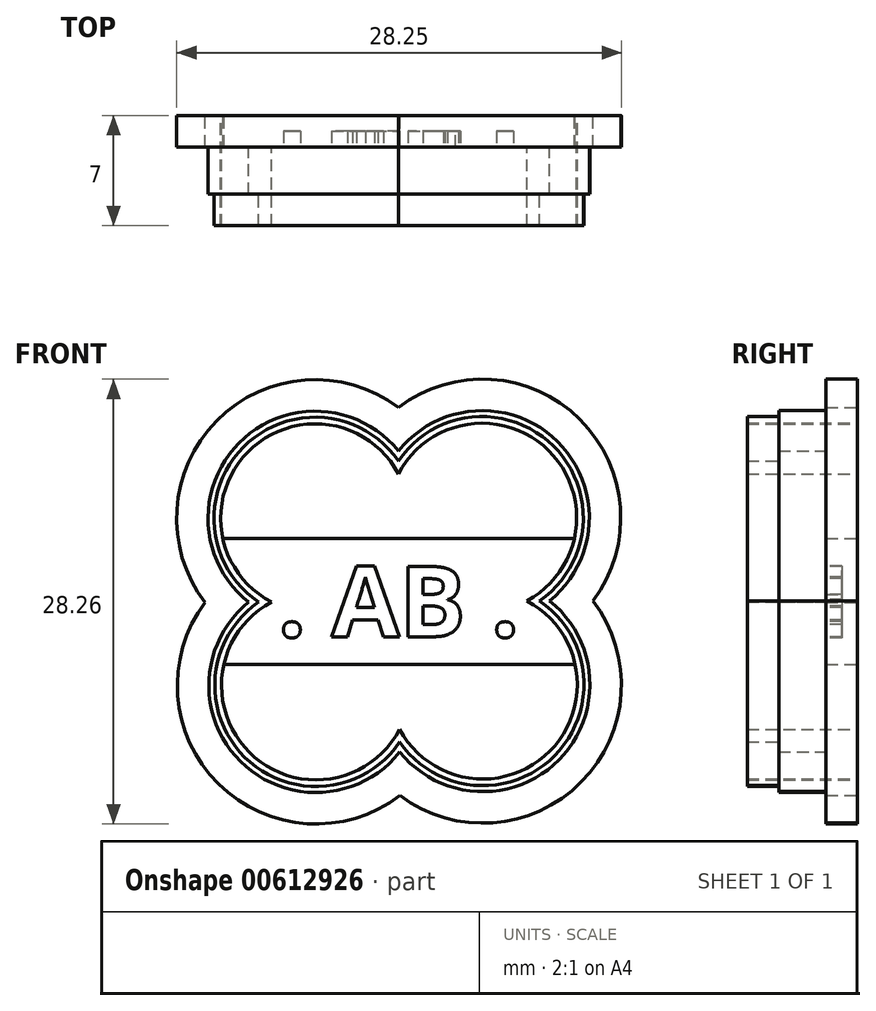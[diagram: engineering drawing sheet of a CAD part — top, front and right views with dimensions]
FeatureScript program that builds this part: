
annotation { "Feature Type Name" : "Feature", "Feature Type Description" : "" }
export const myFeature = defineFeature(function(context is Context, id is Id, definition is map)
    precondition{}
    {
        {
            var Q0;
            Q0=qCreatedBy(makeId("Front.planeOp"),FACE);
            var sketch = newSketch(context, id + "F0", { "sketchPlane" : qUnion([Q0])});
            skArc(sketch, "E0", {"start": v(-0.03, 8.1) * mm, "mid": v(-9.59, 9.5) * mm, "end": v(-8.1, -0.04) * mm});
            skArc(sketch, "E1", {"start": v(-8.1, -0.04) * mm, "mid": v(-9.5, -9.6) * mm, "end": v(0.04, -8.12) * mm});
            skArc(sketch, "E2.trimOffspring", {"start": v(8.12, 0.03) * mm, "mid": v(9.5, 9.58) * mm, "end": v(-0.03, 8.1) * mm});
            skArc(sketch, "E3.trimOffspring", {"start": v(0.04, -8.12) * mm, "mid": v(9.59, -9.5) * mm, "end": v(8.12, 0.03) * mm});
            skArc(sketch, "E4.0", {"start": v(-0.03, 8.92) * mm, "mid": v(-9.89, 9.8) * mm, "end": v(-8.9, -0.04) * mm});
            skArc(sketch, "E4.1", {"start": v(8.93, 0.03) * mm, "mid": v(9.8, 9.88) * mm, "end": v(-0.03, 8.92) * mm});
            skArc(sketch, "E4.2", {"start": v(0.05, -8.93) * mm, "mid": v(9.89, -9.8) * mm, "end": v(8.93, 0.03) * mm});
            skArc(sketch, "E4.3", {"start": v(-8.9, -0.04) * mm, "mid": v(-9.8, -9.9) * mm, "end": v(0.05, -8.93) * mm});
            skSolve(sketch);
        }
        {
            var Q0;
            Q0=qSketchRegion(id+"F0",true);
            extrude(context, id + "F1", {"entities" : qUnion([Q0]), "depth" : 7 * mm, "offsetDistance" : 25 * mm});
        }
        {
            var Q0;
            Q0=qCreatedBy(makeId("Front.planeOp"),FACE);
            var sketch = newSketch(context, id + "F2", { "sketchPlane" : qUnion([Q0])});
            skArc(sketch, "E5.0", {"start": v(-9.55, -0.05) * mm, "mid": v(-10.06, -10.16) * mm, "end": v(0.05, -9.57) * mm});
            skArc(sketch, "E5.1", {"start": v(-0.03, 9.56) * mm, "mid": v(-10.15, 10.07) * mm, "end": v(-9.55, -0.05) * mm});
            skArc(sketch, "E5.2", {"start": v(9.57, 0.04) * mm, "mid": v(10.07, 10.15) * mm, "end": v(-0.03, 9.56) * mm});
            skArc(sketch, "E5.3", {"start": v(0.05, -9.57) * mm, "mid": v(10.16, -10.07) * mm, "end": v(9.57, 0.04) * mm});
            skSolve(sketch);
        }
        {
            var Q0;
            Q0=qSketchRegion(id+"F2",true);
            extrude(context, id + "F3", {"entities" : qUnion([Q0]), "operationType" : NewBodyOperationType.ADD, "depth" : 5 * mm, "offsetDistance" : 25 * mm});
        }
        {
            var Q0;
            Q0=makeQuery(id+"F3.boolean.opBoolean","SPLIT",FACE,{"disambiguationData":[TD([makeQuery(id+"F1.opExtrude","SWEPT_FACE",FACE,{"disambiguationData":[OSD([sQuery(id+"F0.wireOp",EDGE,"E0")])]})])],"derivedFrom":makeQuery(id+"F3.opExtrude","CAP_FACE",FACE,{"disambiguationData":[OSD([sQuery(id+"F2.wireOp",EDGE,"E5.0"),sQuery(id+"F2.wireOp",EDGE,"E5.1"),sQuery(id+"F2.wireOp",EDGE,"E5.2"),sQuery(id+"F2.wireOp",EDGE,"E5.3")])],"isStart":false})});
            var sketch = newSketch(context, id + "F4", { "sketchPlane" : qUnion([Q0])});
            skSolve(sketch);
        }
        {
            var Q0;
            {var subQ0=makeQuery(id+"F3.opExtrude","CAP_FACE",FACE,{"disambiguationData":[OSD([sQuery(id+"F2.wireOp",EDGE,"E5.0"),sQuery(id+"F2.wireOp",EDGE,"E5.1"),sQuery(id+"F2.wireOp",EDGE,"E5.2"),sQuery(id+"F2.wireOp",EDGE,"E5.3")])],"isStart":false});Q0=makeQuery(id+"F4.imprint","IMPRINT",FACE,{"disambiguationData":[TD([[makeQuery(id+"F4.imprint","IMPRINT",EDGE,{"derivedFrom":makeQuery(id+"F3.boolean.opBoolean","INTERSECT",EDGE,{"derivedFrom":[makeQuery(id+"F1.opExtrude","SWEPT_FACE",FACE,{"disambiguationData":[OSD([sQuery(id+"F0.wireOp",EDGE,"E0")])]}),subQ0]})}),1.0]])]});}
            extrude(context, id + "F5", {"entities" : qUnion([Q0]), "operationType" : NewBodyOperationType.REMOVE, "oppositeDirection" : true, "depth" : 8 * mm, "offsetDistance" : 25 * mm});
        }
        {
            var Q0;
            Q0=qCreatedBy(makeId("Front.planeOp"),FACE);
            var sketch = newSketch(context, id + "F6", { "sketchPlane" : qUnion([Q0])});
            skArc(sketch, "E6.0", {"start": v(-12.31, -0.06) * mm, "mid": v(-11.47, -11.59) * mm, "end": v(0.07, -12.33) * mm});
            skArc(sketch, "E6.1", {"start": v(-0.04, 12.32) * mm, "mid": v(-11.57, 11.48) * mm, "end": v(-12.31, -0.06) * mm});
            skArc(sketch, "E6.2", {"start": v(12.33, 0.05) * mm, "mid": v(11.48, 11.57) * mm, "end": v(-0.04, 12.32) * mm});
            skArc(sketch, "E6.3", {"start": v(0.07, -12.33) * mm, "mid": v(11.58, -11.47) * mm, "end": v(12.33, 0.05) * mm});
            skSolve(sketch);
        }
        {
            var Q0;
            Q0=qSketchRegion(id+"F6",true);
            extrude(context, id + "F7", {"entities" : qUnion([Q0]), "operationType" : NewBodyOperationType.ADD, "depth" : 2 * mm, "offsetDistance" : 25 * mm});
        }
        {
            var Q0;
            {var subQ3=sQuery(id+"F0.wireOp",EDGE,"E0");Q0=makeQuery(id+"F7.boolean.opBoolean","SPLIT",FACE,{"disambiguationData":[TD([makeQuery(id+"F1.opExtrude","SWEPT_FACE",FACE,{"disambiguationData":[OSD([subQ3])]})])],"derivedFrom":makeQuery(id+"F7.opExtrude","CAP_FACE",FACE,{"disambiguationData":[OSD([sQuery(id+"F6.wireOp",EDGE,"E6.0"),sQuery(id+"F6.wireOp",EDGE,"E6.1"),sQuery(id+"F6.wireOp",EDGE,"E6.2"),sQuery(id+"F6.wireOp",EDGE,"E6.3")])],"isStart":false})});}
            var sketch = newSketch(context, id + "F8", { "sketchPlane" : qUnion([Q0])});
            skSolve(sketch);
        }
        {
            var Q0;
            {var subQ0=makeQuery(id+"F7.opExtrude","CAP_FACE",FACE,{"disambiguationData":[OSD([sQuery(id+"F6.wireOp",EDGE,"E6.0"),sQuery(id+"F6.wireOp",EDGE,"E6.1"),sQuery(id+"F6.wireOp",EDGE,"E6.2"),sQuery(id+"F6.wireOp",EDGE,"E6.3")])],"isStart":false});var subQ1=sQuery(id+"F2.wireOp",EDGE,"E5.3");var subQ2=sQuery(id+"F2.wireOp",EDGE,"E5.2");var subQ3=sQuery(id+"F2.wireOp",EDGE,"E5.1");var subQ4=sQuery(id+"F2.wireOp",EDGE,"E5.0");var subQ5=sQuery(id+"F0.wireOp",EDGE,"E0");Q0=makeQuery(id+"F8.imprint","IMPRINT",FACE,{"disambiguationData":[TD([[makeQuery(id+"F8.imprint","IMPRINT",EDGE,{"derivedFrom":makeQuery(id+"F7.boolean.opBoolean","INTERSECT",EDGE,{"derivedFrom":[makeQuery(id+"F5.boolean.opBoolean","MERGE",FACE,{"derivedFrom":[makeQuery(id+"F1.opExtrude","SWEPT_FACE",FACE,{"disambiguationData":[OSD([subQ5])]}),makeQuery(id+"F5.opExtrude","SWEPT_FACE",FACE,{"disambiguationData":[OSD([subQ5,subQ4,subQ3,subQ2,subQ1])]})]}),subQ0]})}),1.0]])]});}
            cPlane(context, id + "F9", {"entities" : qUnion([Q0]), "cplaneType" : CPlaneType.OFFSET, "offset" : 0 * mm, "width" : 150 * mm, "height" : 150 * mm});
        }
        {
            var Q0;
            {var subQ0=makeQuery(id+"F7.opExtrude","CAP_FACE",FACE,{"disambiguationData":[OSD([sQuery(id+"F6.wireOp",EDGE,"E6.0"),sQuery(id+"F6.wireOp",EDGE,"E6.1"),sQuery(id+"F6.wireOp",EDGE,"E6.2"),sQuery(id+"F6.wireOp",EDGE,"E6.3")])],"isStart":false});var subQ1=sQuery(id+"F2.wireOp",EDGE,"E5.3");var subQ2=sQuery(id+"F2.wireOp",EDGE,"E5.2");var subQ3=sQuery(id+"F2.wireOp",EDGE,"E5.1");var subQ4=sQuery(id+"F2.wireOp",EDGE,"E5.0");var subQ5=sQuery(id+"F0.wireOp",EDGE,"E0");Q0=makeQuery(id+"F8.imprint","IMPRINT",FACE,{"disambiguationData":[TD([[makeQuery(id+"F8.imprint","IMPRINT",EDGE,{"derivedFrom":makeQuery(id+"F7.boolean.opBoolean","INTERSECT",EDGE,{"derivedFrom":[makeQuery(id+"F5.boolean.opBoolean","MERGE",FACE,{"derivedFrom":[makeQuery(id+"F1.opExtrude","SWEPT_FACE",FACE,{"disambiguationData":[OSD([subQ5])]}),makeQuery(id+"F5.opExtrude","SWEPT_FACE",FACE,{"disambiguationData":[OSD([subQ5,subQ4,subQ3,subQ2,subQ1])]})]}),subQ0]})}),1.0]])]});}
            extrude(context, id + "F10", {"entities" : qUnion([Q0]), "operationType" : NewBodyOperationType.REMOVE, "oppositeDirection" : true, "depth" : 2 * mm, "offsetDistance" : 25 * mm});
        }
        {
            var Q0;
            Q0=qCreatedBy(id+"F9.planeOp",FACE);
            var sketch = newSketch(context, id + "F11", { "sketchPlane" : qUnion([Q0])});
            skLineSegment(sketch, "E7.bottom", {"start": v(-11.92, 0) * mm, "end": v(11.56, 0) * mm});
            skLineSegment(sketch, "E7.top", {"start": v(-11.92, 4) * mm, "end": v(11.56, 4) * mm});
            skLineSegment(sketch, "E7.left", {"start": v(-11.92, 0) * mm, "end": v(-11.92, 4) * mm});
            skLineSegment(sketch, "E7.right", {"start": v(11.56, 0) * mm, "end": v(11.56, 4) * mm});
            skLineSegment(sketch, "E8.top", {"start": v(-11.92, -4) * mm, "end": v(11.56, -4) * mm});
            skLineSegment(sketch, "E8.left", {"start": v(-11.92, 0) * mm, "end": v(-11.92, -4) * mm});
            skLineSegment(sketch, "E8.right", {"start": v(11.56, 0) * mm, "end": v(11.56, -4) * mm});
            skLineSegment(sketch, "E9.bottom", {"start": v(0, 11.34) * mm, "end": v(-4, 11.34) * mm});
            skLineSegment(sketch, "E10.bottom", {"start": v(0, 11.34) * mm, "end": v(4, 11.34) * mm});
            skSolve(sketch);
        }
        {
            var Q0;
            Q0=qSketchRegion(id+"F11",true);
            extrude(context, id + "F12", {"entities" : qUnion([Q0]), "operationType" : NewBodyOperationType.ADD, "oppositeDirection" : true, "depth" : 2 * mm, "offsetDistance" : 25 * mm});
        }
        {
            var Q0;
            Q0=makeQuery(id+"F12.opExtrude","CAP_FACE",FACE,{"disambiguationData":[OSD([sQuery(id+"F11.wireOp",EDGE,"E7.top"),sQuery(id+"F11.wireOp",EDGE,"E7.left"),sQuery(id+"F11.wireOp",EDGE,"E7.right"),sQuery(id+"F11.wireOp",EDGE,"E8.top"),sQuery(id+"F11.wireOp",EDGE,"E8.left"),sQuery(id+"F11.wireOp",EDGE,"E8.right"),sQuery(id+"F11.wireOp",EDGE,"E9.bottom"),sQuery(id+"F11.wireOp",EDGE,"E9.top"),sQuery(id+"F11.wireOp",EDGE,"E9.left"),sQuery(id+"F11.wireOp",EDGE,"E9.right"),sQuery(id+"F11.wireOp",EDGE,"E10.bottom"),sQuery(id+"F11.wireOp",EDGE,"E10.top"),sQuery(id+"F11.wireOp",EDGE,"E10.right")])],"isStart":true});
            cPlane(context, id + "F13", {"entities" : qUnion([Q0]), "cplaneType" : CPlaneType.OFFSET, "offset" : 0 * mm, "width" : 150 * mm, "height" : 150 * mm});
        }
        {
            var Q0;
            Q0=qCreatedBy(id+"F13.planeOp",FACE);
            var sketch = newSketch(context, id + "F14", { "sketchPlane" : qUnion([Q0])});
            skText(sketch, "E11", { "text": ". AB .", "fontName": "OpenSans-Bold.ttf"});
            const initialGuessF14  = {"E11": [-0.00769, -0.00224, 1, 0, 0.0045]};
            skSetInitialGuess(sketch, initialGuessF14);
            skSolve(sketch);
        }
        {
            var Q0;
            Q0=qSketchRegion(id+"F14",true);
            extrude(context, id + "F15", {"entities" : qUnion([Q0]), "operationType" : NewBodyOperationType.REMOVE, "oppositeDirection" : true, "depth" : 1 * mm, "offsetDistance" : 25 * mm});
        }
    });
